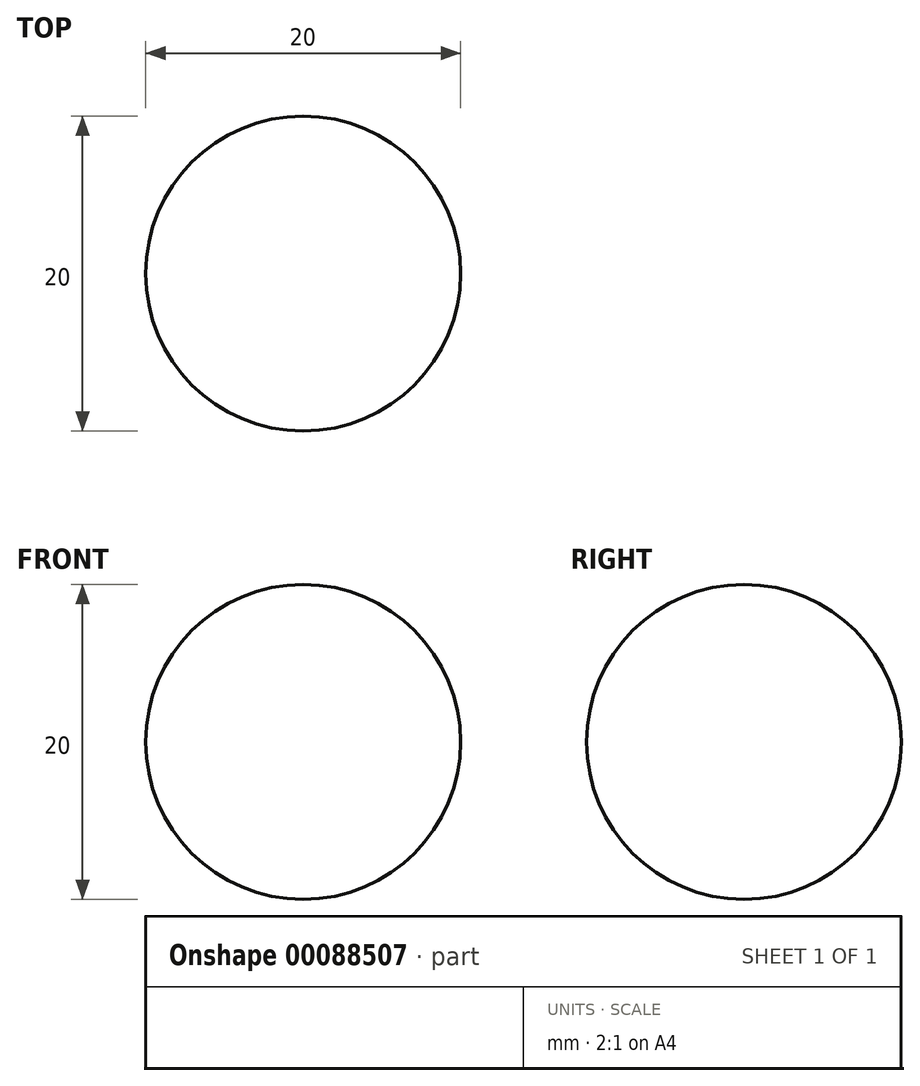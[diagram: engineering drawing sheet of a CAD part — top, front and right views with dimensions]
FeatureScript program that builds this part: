
annotation { "Feature Type Name" : "Feature", "Feature Type Description" : "" }
export const myFeature = defineFeature(function(context is Context, id is Id, definition is map)
    precondition{}
    {
        {
            var Q0;
            Q0=qCreatedBy(makeId("Front.planeOp"),FACE);
            var sketch = newSketch(context, id + "F0", { "sketchPlane" : qUnion([Q0])});
            skLineSegment(sketch, "E0", {"start": v(0, 0) * mm, "end": v(0, 10) * mm});
            skLineSegment(sketch, "E1", {"start": v(0, 0) * mm, "end": v(0, -10) * mm});
            skArc(sketch, "E2", {"start": v(0, 10) * mm, "mid": v(10, 0) * mm, "end": v(0, -10) * mm});
            skSolve(sketch);
        }
        {
            var Q0;
            Q0=makeQuery(id+"F0.imprint","IMPRINT",FACE,{"disambiguationData":[TD([[makeQuery(id+"F0.imprint","IMPRINT",EDGE,{"derivedFrom":sQuery(id+"F0.wireOp",EDGE,"E0")}),-1.0]])]});
            var Q1;
            Q1=sQuery(id+"F0.wireOp",EDGE,"E0");
            revolve(context, id + "F1", {"entities" : qUnion([Q0]), "axis" : qUnion([Q1]), "revolveType" : RevolveType.FULL});
        }
    });
